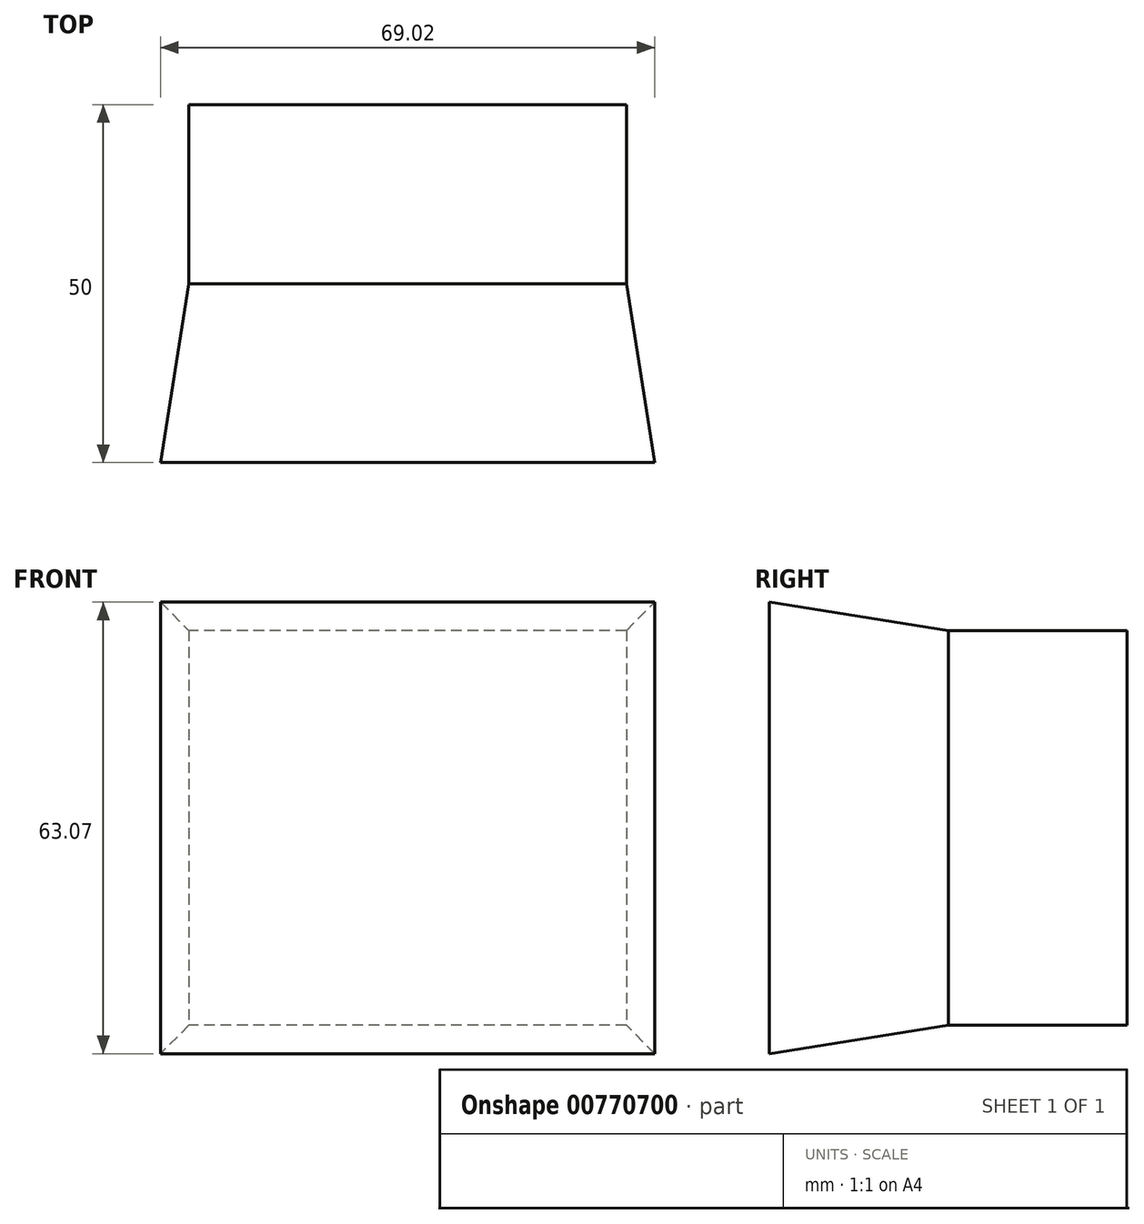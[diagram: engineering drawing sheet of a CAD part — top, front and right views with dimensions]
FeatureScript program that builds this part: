
annotation { "Feature Type Name" : "Feature", "Feature Type Description" : "" }
export const myFeature = defineFeature(function(context is Context, id is Id, definition is map)
    precondition{}
    {
        {
            var Q0;
            Q0=qCreatedBy(makeId("Front.planeOp"),FACE);
            var sketch = newSketch(context, id + "F0", { "sketchPlane" : qUnion([Q0])});
            skLineSegment(sketch, "E0.bottom", {"start": v(0, 99.93) * mm, "end": v(-61.1, 99.93) * mm});
            skLineSegment(sketch, "E0.top", {"start": v(0, 44.78) * mm, "end": v(-61.1, 44.78) * mm});
            skLineSegment(sketch, "E0.left", {"start": v(0, 99.93) * mm, "end": v(0, 44.78) * mm});
            skLineSegment(sketch, "E0.right", {"start": v(-61.1, 99.93) * mm, "end": v(-61.1, 44.78) * mm});
            skPoint(sketch, "E0.middle", {"position": v(-30.55, 72.36) * mm});
            skSolve(sketch);
        }
        {
            var Q0;
            Q0 = qSketchRegion(id + "F0", true);
            extrude(context, id + "F1", {"entities" : qUnion([Q0]), "depth" : 25 * mm, "offsetDistance" : 25 * mm, "hasDraft" : true, "draftAngle" : 9 * degree, "hasSecondDirection" : true, "secondDirectionOppositeDirection" : true, "secondDirectionDepth" : 25 * mm});
        }
    });
